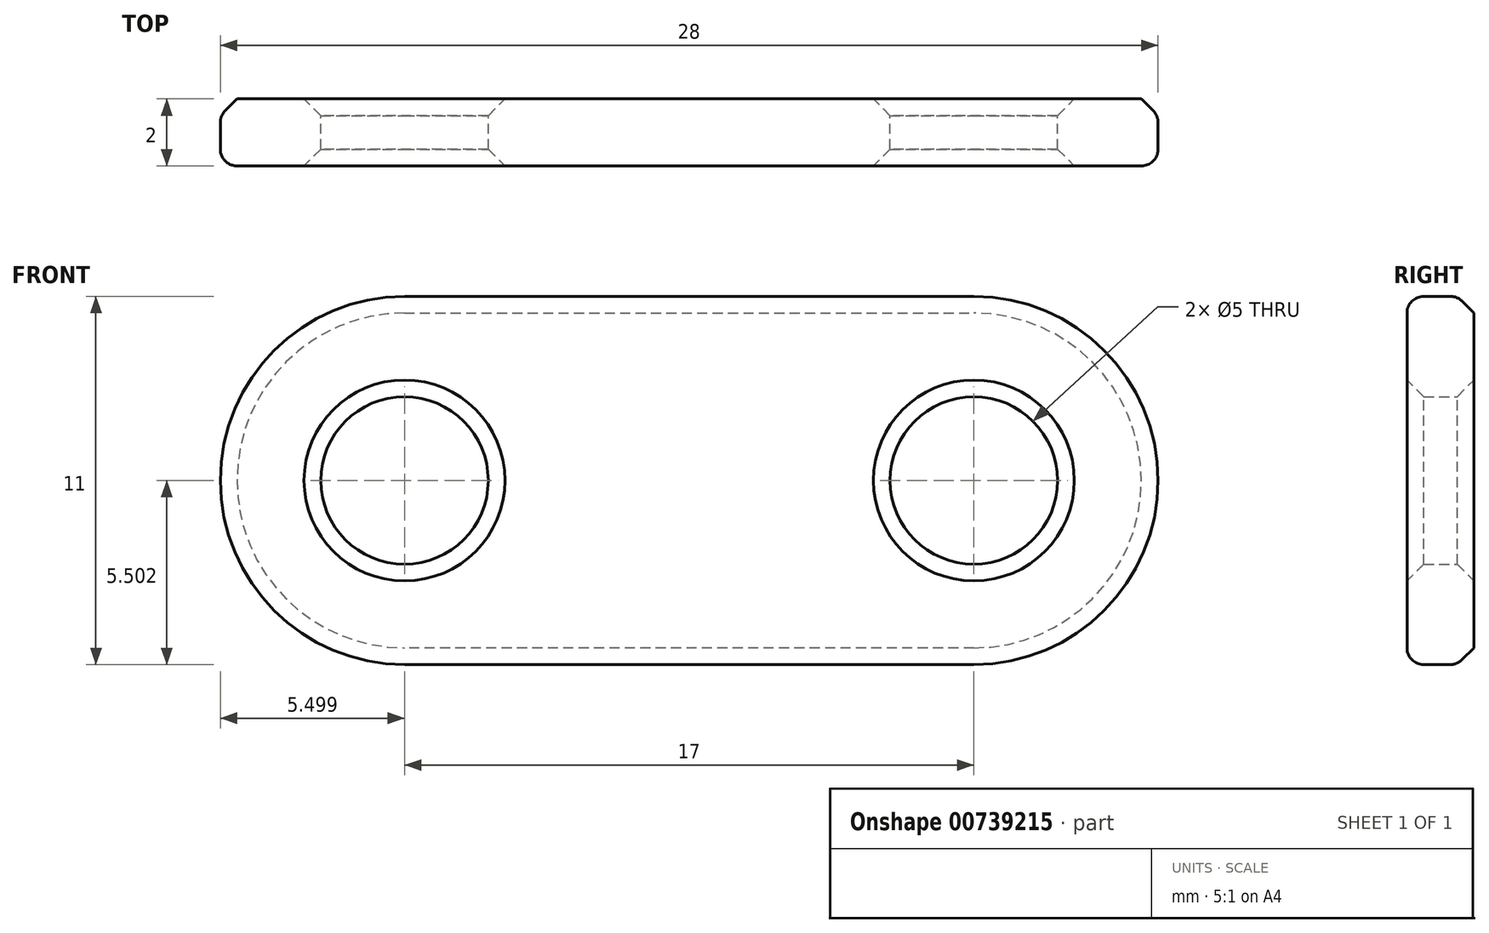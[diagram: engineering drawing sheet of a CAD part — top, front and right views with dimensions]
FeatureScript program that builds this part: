
annotation { "Feature Type Name" : "Feature", "Feature Type Description" : "" }
export const myFeature = defineFeature(function(context is Context, id is Id, definition is map)
    precondition{}
    {
        {
            var Q0;
            Q0=qCreatedBy(makeId("Front.planeOp"),FACE);
            var sketch = newSketch(context, id + "F0", { "sketchPlane" : qUnion([Q0])});
            skLineSegment(sketch, "E0", {"start": v(-9.88, 7.45) * mm, "end": v(7.12, 7.45) * mm});
            skLineSegment(sketch, "E1", {"start": v(7.12, -3.55) * mm, "end": v(-9.88, -3.55) * mm});
            skArc(sketch, "E2", {"start": v(-9.88, 7.45) * mm, "mid": v(-15.38, 1.95) * mm, "end": v(-9.88, -3.55) * mm});
            skArc(sketch, "E3", {"start": v(7.12, -3.55) * mm, "mid": v(12.62, 1.95) * mm, "end": v(7.12, 7.45) * mm});
            skCircle(sketch, "E4", {"center": v(-9.88, 1.95) * mm, "radius": 2.5 * mm});
            skCircle(sketch, "E5", {"center": v(7.12, 1.95) * mm, "radius": 2.5 * mm});
            skSolve(sketch);
        }
        {
            var Q0;
            Q0 = qSketchRegion(id + "F0", true);
            extrude(context, id + "F1", {"entities" : qUnion([Q0]), "depth" : 2 * mm, "offsetDistance" : 25.4 * mm});
        }
        {
            var Q0;
            Q0=makeQuery(id+"F1.opExtrude","CAP_EDGE",EDGE,{"disambiguationData":[OSD([sQuery(id+"F0.wireOp",EDGE,"E0")])],"isStart":false});
            fillet(context, id + "F2", {"entities" : qUnion([Q0]), "radius" : 0.5 * mm, "tangentPropagation" : true, "allowEdgeOverflow" : false});
        }
        {
            var Q0;
            Q0=makeQuery(id+"F1.opExtrude","CAP_EDGE",EDGE,{"disambiguationData":[OSD([sQuery(id+"F0.wireOp",EDGE,"E4")])],"isStart":false});
            var Q1;
            Q1=makeQuery(id+"F1.opExtrude","CAP_EDGE",EDGE,{"disambiguationData":[OSD([sQuery(id+"F0.wireOp",EDGE,"E5")])],"isStart":false});
            chamfer(context, id + "F3", {"entities" : qUnion([Q0, Q1]), "width" : 0.5 * mm, "tangentPropagation" : true});
        }
        {
            var Q0;
            Q0=makeQuery(id+"F1.opExtrude","CAP_EDGE",EDGE,{"disambiguationData":[OSD([sQuery(id+"F0.wireOp",EDGE,"E4")])],"isStart":true});
            var Q1;
            Q1=makeQuery(id+"F1.opExtrude","CAP_FACE",FACE,{"disambiguationData":[OSD([sQuery(id+"F0.wireOp",EDGE,"E0"),sQuery(id+"F0.wireOp",EDGE,"E1"),sQuery(id+"F0.wireOp",EDGE,"E2"),sQuery(id+"F0.wireOp",EDGE,"E3"),sQuery(id+"F0.wireOp",EDGE,"E4"),sQuery(id+"F0.wireOp",EDGE,"E5")])],"isStart":true});
            chamfer(context, id + "F4", {"entities" : qUnion([Q0, Q1]), "width" : 0.5 * mm, "tangentPropagation" : true});
        }
        {
            var Q0;
            {var subQ0=sQuery(id+"F0.wireOp",EDGE,"E1");Q0=makeQuery(id+"F4.opChamfer","BLEND_EDGE",EDGE,{"blendedFrom":[makeQuery(id+"F1.opExtrude","CAP_EDGE",EDGE,{"disambiguationData":[OSD([subQ0])],"isStart":true}),makeQuery(id+"F1.opExtrude","SWEPT_FACE",FACE,{"disambiguationData":[OSD([subQ0])]})],"blendedInto":[makeQuery(id+"F1.opExtrude","SWEPT_FACE",FACE,{"disambiguationData":[OSD([subQ0])]})]});}
            fillet(context, id + "F5", {"entities" : qUnion([Q0]), "radius" : 0.5 * mm, "tangentPropagation" : true, "allowEdgeOverflow" : false});
        }
    });
